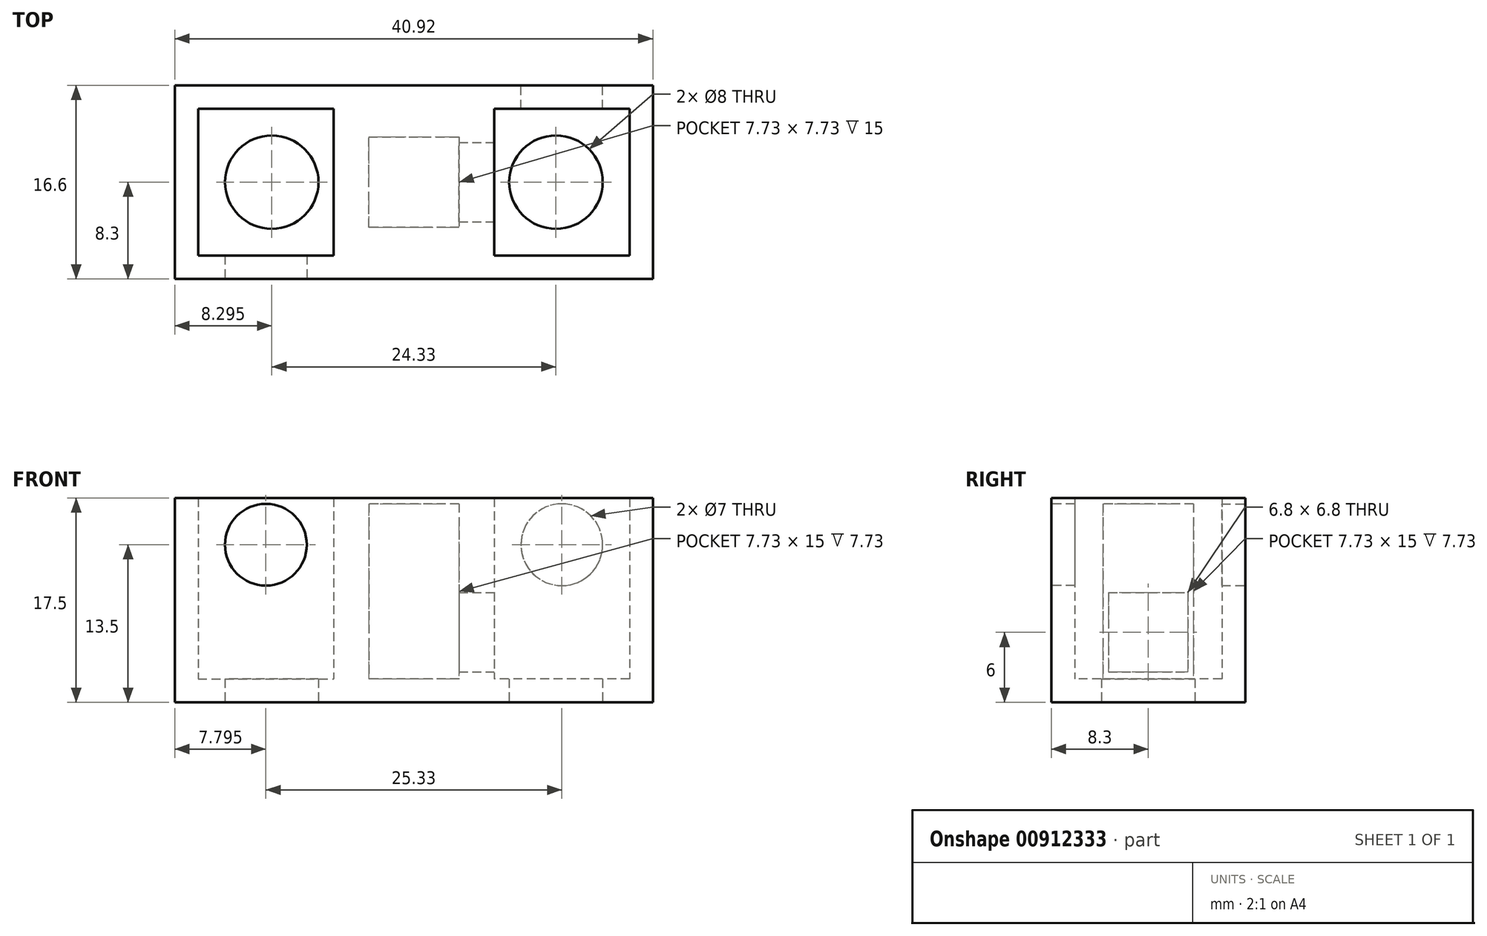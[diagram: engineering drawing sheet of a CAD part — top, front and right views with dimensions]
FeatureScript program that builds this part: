
annotation { "Feature Type Name" : "Feature", "Feature Type Description" : "" }
export const myFeature = defineFeature(function(context is Context, id is Id, definition is map)
    precondition{}
    {
        {
            var Q0;
            Q0=qCreatedBy(makeId("Top.planeOp"),FACE);
            var sketch = newSketch(context, id + "F0", { "sketchPlane" : qUnion([Q0])});
            skLineSegment(sketch, "E0.bottom", {"start": v(-3.17, 3.17) * mm, "end": v(3.16, 3.17) * mm});
            skLineSegment(sketch, "E0.top", {"start": v(-3.17, -3.17) * mm, "end": v(3.17, -3.17) * mm});
            skLineSegment(sketch, "E0.left", {"start": v(-3.17, 3.17) * mm, "end": v(-3.17, -3.17) * mm});
            skLineSegment(sketch, "E0.right", {"start": v(3.17, 3.17) * mm, "end": v(3.17, -3.17) * mm});
            skLineSegment(sketch, "E1", {"start": v(-3.17, 0) * mm, "end": v(3.17, 0) * mm, "construction": true});
            skLineSegment(sketch, "E2", {"start": v(-3.17, 3.17) * mm, "end": v(-3.87, 3.17) * mm, "construction": true});
            skLineSegment(sketch, "E3", {"start": v(-3.17, 3.17) * mm, "end": v(-3.17, 3.86) * mm, "construction": true});
            skLineSegment(sketch, "E4", {"start": v(-3.87, 3.86) * mm, "end": v(3.86, 3.86) * mm});
            skLineSegment(sketch, "E5", {"start": v(3.86, 3.86) * mm, "end": v(3.86, -3.86) * mm});
            skLineSegment(sketch, "E6", {"start": v(3.86, -3.86) * mm, "end": v(-3.86, -3.86) * mm});
            skLineSegment(sketch, "E7", {"start": v(-3.86, -3.86) * mm, "end": v(-3.87, 3.87) * mm});
            skLineSegment(sketch, "E8", {"start": v(3.17, -3.17) * mm, "end": v(3.17, -3.86) * mm, "construction": true});
            skLineSegment(sketch, "E9", {"start": v(-3.87, 3.17) * mm, "end": v(-6.87, 3.17) * mm, "construction": true});
            skLineSegment(sketch, "E10", {"start": v(3.17, -3.86) * mm, "end": v(3.17, -6.87) * mm, "construction": true});
            skLineSegment(sketch, "E11", {"start": v(-3.17, 3.86) * mm, "end": v(-3.17, 6.87) * mm, "construction": true});
            skLineSegment(sketch, "E12", {"start": v(-6.87, 6.87) * mm, "end": v(6.86, 6.87) * mm});
            skLineSegment(sketch, "E13", {"start": v(6.86, 6.87) * mm, "end": v(6.86, -6.87) * mm});
            skLineSegment(sketch, "E14", {"start": v(6.86, -6.87) * mm, "end": v(-6.87, -6.87) * mm});
            skLineSegment(sketch, "E15", {"start": v(-6.86, -6.86) * mm, "end": v(-6.87, 6.86) * mm});
            skLineSegment(sketch, "E16", {"start": v(-12.17, 5.3) * mm, "end": v(-12.17, -5.3) * mm, "construction": true});
            skLineSegment(sketch, "E17", {"start": v(-17.46, 0) * mm, "end": v(-6.87, 0) * mm, "construction": true});
            skLineSegment(sketch, "E18", {"start": v(0, 3.17) * mm, "end": v(0, -3.17) * mm, "construction": true});
            skCircle(sketch, "E19", {"center": v(-12.17, 0) * mm, "radius": 4 * mm});
            skLineSegment(sketch, "E20", {"start": v(0, 0) * mm, "end": v(-6.86, 0) * mm, "construction": true});
            skLineSegment(sketch, "E21.bottom", {"start": v(-17.46, 5.3) * mm, "end": v(-6.87, 5.3) * mm});
            skLineSegment(sketch, "E21.top", {"start": v(-17.46, -5.3) * mm, "end": v(-6.86, -5.3) * mm});
            skLineSegment(sketch, "E21.left", {"start": v(-17.46, 5.3) * mm, "end": v(-17.46, -5.3) * mm});
            skLineSegment(sketch, "E21.right", {"start": v(-6.87, 5.3) * mm, "end": v(-6.86, -5.3) * mm});
            skLineSegment(sketch, "E22", {"start": v(-17.46, 5.3) * mm, "end": v(-17.46, 6.3) * mm, "construction": true});
            skLineSegment(sketch, "E23", {"start": v(-17.46, 5.3) * mm, "end": v(-18.47, 5.3) * mm, "construction": true});
            skLineSegment(sketch, "E24", {"start": v(-18.47, 6.3) * mm, "end": v(-18.47, -6.3) * mm});
            skLineSegment(sketch, "E25", {"start": v(-18.47, 6.3) * mm, "end": v(-6.87, 6.3) * mm});
            skLineSegment(sketch, "E26", {"start": v(-6.87, 6.3) * mm, "end": v(-6.87, 6.87) * mm});
            skLineSegment(sketch, "E27.MirrorCS", {"start": v(-18.47, -6.3) * mm, "end": v(-6.86, -6.3) * mm});
            skLineSegment(sketch, "E28", {"start": v(-6.86, -6.3) * mm, "end": v(-6.86, -6.86) * mm});
            skLineSegment(sketch, "E29", {"start": v(-18.47, 6.3) * mm, "end": v(-18.47, 8.3) * mm, "construction": true});
            skLineSegment(sketch, "E30", {"start": v(-18.47, 6.3) * mm, "end": v(-20.47, 6.3) * mm, "construction": true});
            skLineSegment(sketch, "E31", {"start": v(-20.47, 8.3) * mm, "end": v(20.47, 8.3) * mm});
            skLineSegment(sketch, "E32", {"start": v(-20.47, 8.3) * mm, "end": v(-20.47, -8.3) * mm});
            skLineSegment(sketch, "E33", {"start": v(-18.47, -6.3) * mm, "end": v(-18.47, -8.3) * mm, "construction": true});
            skLineSegment(sketch, "E34.MirrorCS", {"start": v(6.86, 6.3) * mm, "end": v(6.86, 6.87) * mm});
            skLineSegment(sketch, "E35.MirrorCS", {"start": v(18.47, 6.3) * mm, "end": v(6.86, 6.3) * mm});
            skLineSegment(sketch, "E36.MirrorCS", {"start": v(18.47, 6.3) * mm, "end": v(18.47, -6.3) * mm});
            skLineSegment(sketch, "E37.MirrorCS", {"start": v(18.47, -6.3) * mm, "end": v(6.86, -6.3) * mm});
            skLineSegment(sketch, "E38.MirrorCS", {"start": v(6.87, -6.3) * mm, "end": v(6.87, -6.86) * mm});
            skLineSegment(sketch, "E39.MirrorCS", {"start": v(17.46, -5.3) * mm, "end": v(6.86, -5.3) * mm});
            skLineSegment(sketch, "E40.MirrorCS", {"start": v(17.46, 5.3) * mm, "end": v(17.47, -5.3) * mm});
            skCircle(sketch, "E41.MirrorC", {"center": v(12.17, 0) * mm, "radius": 4 * mm});
            skLineSegment(sketch, "E42.MirrorCS", {"start": v(17.46, 5.3) * mm, "end": v(6.86, 5.3) * mm});
            skLineSegment(sketch, "E43.MirrorCS", {"start": v(20.47, 8.3) * mm, "end": v(20.47, -8.3) * mm});
            skLineSegment(sketch, "E44.MirrorCS", {"start": v(-20.47, -8.3) * mm, "end": v(20.47, -8.3) * mm});
            skSolve(sketch);
        }
        {
            var Q0;
            {var subQ0=sQuery(id+"F0.wireOp",EDGE,"E39.MirrorCS");Q0=makeQuery(id+"F0.imprint","IMPRINT",FACE,{"disambiguationData":[TD([[makeQuery(id+"F0.imprint","IMPRINT",EDGE,{"derivedFrom":subQ0}),-1.0]])]});}
            var Q1;
            {var subQ0=sQuery(id+"F0.wireOp",EDGE,"E34.MirrorCS");Q1=makeQuery(id+"F0.imprint","IMPRINT",FACE,{"disambiguationData":[TD([[makeQuery(id+"F0.imprint","IMPRINT",EDGE,{"derivedFrom":subQ0}),-1.0]])]});}
            var Q2;
            Q2=makeQuery(id+"F0.imprint","IMPRINT",FACE,{"disambiguationData":[TD([[makeQuery(id+"F0.imprint","IMPRINT",EDGE,{"derivedFrom":sQuery(id+"F0.wireOp",EDGE,"E12")}),1.0]])]});
            var Q3;
            {var subQ1=sQuery(id+"F0.wireOp",EDGE,"E21.bottom");Q3=makeQuery(id+"F0.imprint","IMPRINT",FACE,{"disambiguationData":[TD([[makeQuery(id+"F0.imprint","IMPRINT",EDGE,{"derivedFrom":subQ1}),1.0]])]});}
            var Q4;
            Q4=makeQuery(id+"F0.imprint","IMPRINT",FACE,{"disambiguationData":[TD([[makeQuery(id+"F0.imprint","IMPRINT",EDGE,{"derivedFrom":sQuery(id+"F0.wireOp",EDGE,"E19")}),-1.0]])]});
            var Q5;
            Q5=makeQuery(id+"F0.imprint","IMPRINT",FACE,{"disambiguationData":[TD([[makeQuery(id+"F0.imprint","IMPRINT",EDGE,{"derivedFrom":sQuery(id+"F0.wireOp",EDGE,"E4")}),1.0]])]});
            var Q6;
            Q6=makeQuery(id+"F0.imprint","IMPRINT",FACE,{"disambiguationData":[TD([[makeQuery(id+"F0.imprint","IMPRINT",EDGE,{"derivedFrom":sQuery(id+"F0.wireOp",EDGE,"E0.bottom")}),1.0]])]});
            var Q7;
            Q7=makeQuery(id+"F0.imprint","IMPRINT",FACE,{"disambiguationData":[TD([[makeQuery(id+"F0.imprint","IMPRINT",EDGE,{"derivedFrom":sQuery(id+"F0.wireOp",EDGE,"E0.bottom")}),-1.0]])]});
            var Q8;
            {var subQ0=sQuery(id+"F0.wireOp",EDGE,"E35.MirrorCS");Q8=makeQuery(id+"F0.imprint","IMPRINT",FACE,{"disambiguationData":[TD([[makeQuery(id+"F0.imprint","IMPRINT",EDGE,{"derivedFrom":subQ0}),1.0]])]});}
            extrude(context, id + "F1", {"entities" : qUnion([Q0, Q1, Q2, Q3, Q4, Q5, Q6, Q7, Q8]), "depth" : 2 * mm, "offsetDistance" : 25 * mm});
        }
        {
            var Q0;
            Q0=makeQuery(id+"F1.opExtrude","CAP_FACE",FACE,{"disambiguationData":[OSD([sQuery(id+"F0.wireOp",EDGE,"E19"),sQuery(id+"F0.wireOp",EDGE,"E31"),sQuery(id+"F0.wireOp",EDGE,"E32"),sQuery(id+"F0.wireOp",EDGE,"E41.MirrorC"),sQuery(id+"F0.wireOp",EDGE,"E43.MirrorCS"),sQuery(id+"F0.wireOp",EDGE,"E44.MirrorCS")])],"isStart":false});
            var sketch = newSketch(context, id + "F2", { "sketchPlane" : qUnion([Q0])});
            skLineSegment(sketch, "E45.0", {"start": v(-18.47, 6.3) * mm, "end": v(-18.47, -6.3) * mm});
            skLineSegment(sketch, "E45.1", {"start": v(-18.47, 6.3) * mm, "end": v(-6.87, 6.3) * mm});
            skLineSegment(sketch, "E45.2", {"start": v(-18.47, -6.3) * mm, "end": v(-6.86, -6.3) * mm});
            skLineSegment(sketch, "E45.3", {"start": v(-6.86, -6.86) * mm, "end": v(-6.87, 6.86) * mm});
            skLineSegment(sketch, "E45.4", {"start": v(-6.87, 6.3) * mm, "end": v(-6.87, 6.87) * mm});
            skLineSegment(sketch, "E45.5", {"start": v(-6.86, -6.3) * mm, "end": v(-6.86, -6.86) * mm});
            skLineSegment(sketch, "E45.6", {"start": v(-3.87, 3.86) * mm, "end": v(3.86, 3.86) * mm});
            skLineSegment(sketch, "E45.7", {"start": v(-3.86, -3.86) * mm, "end": v(-3.87, 3.87) * mm});
            skLineSegment(sketch, "E45.8", {"start": v(3.86, -3.86) * mm, "end": v(-3.86, -3.86) * mm});
            skLineSegment(sketch, "E45.9", {"start": v(3.86, 3.86) * mm, "end": v(3.86, -3.86) * mm});
            skLineSegment(sketch, "E45.10", {"start": v(6.86, 6.87) * mm, "end": v(6.86, -6.87) * mm});
            skLineSegment(sketch, "E45.11", {"start": v(18.47, 6.3) * mm, "end": v(6.86, 6.3) * mm});
            skLineSegment(sketch, "E45.12", {"start": v(18.47, 6.3) * mm, "end": v(18.47, -6.3) * mm});
            skLineSegment(sketch, "E45.13", {"start": v(18.47, -6.3) * mm, "end": v(6.86, -6.3) * mm});
            skLineSegment(sketch, "E45.14", {"start": v(6.87, -6.3) * mm, "end": v(6.87, -6.86) * mm});
            skLineSegment(sketch, "E45.15", {"start": v(6.86, 6.3) * mm, "end": v(6.86, 6.87) * mm});
            skLineSegment(sketch, "E46.0", {"start": v(-20.47, 8.3) * mm, "end": v(20.47, 8.3) * mm});
            skLineSegment(sketch, "E46.1", {"start": v(-20.47, 8.3) * mm, "end": v(-20.47, -8.3) * mm});
            skLineSegment(sketch, "E46.2", {"start": v(-20.47, -8.3) * mm, "end": v(20.47, -8.3) * mm});
            skLineSegment(sketch, "E46.3", {"start": v(20.47, 8.3) * mm, "end": v(20.47, -8.3) * mm});
            skSolve(sketch);
        }
        {
            var Q0;
            Q0=makeQuery(id+"F2.imprint","IMPRINT",FACE,{"disambiguationData":[TD([[makeQuery(id+"F2.imprint","IMPRINT",EDGE,{"derivedFrom":sQuery(id+"F2.wireOp",EDGE,"E45.0")}),-1.0]])]});
            extrude(context, id + "F3", {"entities" : qUnion([Q0]), "operationType" : NewBodyOperationType.ADD, "depth" : 15 * mm, "offsetDistance" : 25 * mm});
        }
        {
            var Q0;
            Q0=makeQuery(id+"F3.opExtrude","CAP_FACE",FACE,{"disambiguationData":[OSD([sQuery(id+"F2.wireOp",EDGE,"E45.0"),sQuery(id+"F2.wireOp",EDGE,"E45.1"),sQuery(id+"F2.wireOp",EDGE,"E45.2"),sQuery(id+"F2.wireOp",EDGE,"E45.3"),sQuery(id+"F2.wireOp",EDGE,"E45.4"),sQuery(id+"F2.wireOp",EDGE,"E45.5"),sQuery(id+"F2.wireOp",EDGE,"E45.6"),sQuery(id+"F2.wireOp",EDGE,"E45.7"),sQuery(id+"F2.wireOp",EDGE,"E45.8"),sQuery(id+"F2.wireOp",EDGE,"E45.9"),sQuery(id+"F2.wireOp",EDGE,"E45.10"),sQuery(id+"F2.wireOp",EDGE,"E45.11"),sQuery(id+"F2.wireOp",EDGE,"E45.12"),sQuery(id+"F2.wireOp",EDGE,"E45.13"),sQuery(id+"F2.wireOp",EDGE,"E45.14"),sQuery(id+"F2.wireOp",EDGE,"E45.15"),sQuery(id+"F2.wireOp",EDGE,"E46.0"),sQuery(id+"F2.wireOp",EDGE,"E46.1"),sQuery(id+"F2.wireOp",EDGE,"E46.2"),sQuery(id+"F2.wireOp",EDGE,"E46.3")])],"isStart":false});
            var sketch = newSketch(context, id + "F4", { "sketchPlane" : qUnion([Q0])});
            skLineSegment(sketch, "E47.0", {"start": v(-20.47, 8.3) * mm, "end": v(-20.47, -8.3) * mm});
            skLineSegment(sketch, "E47.1", {"start": v(-20.47, 8.3) * mm, "end": v(20.47, 8.3) * mm});
            skLineSegment(sketch, "E47.2", {"start": v(20.47, 8.3) * mm, "end": v(20.47, -8.3) * mm});
            skLineSegment(sketch, "E47.3", {"start": v(-20.47, -8.3) * mm, "end": v(20.47, -8.3) * mm});
            skLineSegment(sketch, "E47.4", {"start": v(18.47, 6.3) * mm, "end": v(18.47, -6.3) * mm});
            skLineSegment(sketch, "E47.5", {"start": v(18.47, -6.3) * mm, "end": v(6.86, -6.3) * mm});
            skLineSegment(sketch, "E47.6", {"start": v(6.86, 6.87) * mm, "end": v(6.86, -6.87) * mm});
            skLineSegment(sketch, "E47.7", {"start": v(6.87, -6.3) * mm, "end": v(6.87, -6.86) * mm});
            skLineSegment(sketch, "E47.8", {"start": v(18.47, 6.3) * mm, "end": v(6.86, 6.3) * mm});
            skLineSegment(sketch, "E47.9", {"start": v(6.86, 6.3) * mm, "end": v(6.86, 6.87) * mm});
            skLineSegment(sketch, "E47.10", {"start": v(-6.86, -6.86) * mm, "end": v(-6.87, 6.86) * mm});
            skLineSegment(sketch, "E47.11", {"start": v(-18.47, -6.3) * mm, "end": v(-6.86, -6.3) * mm});
            skLineSegment(sketch, "E47.12", {"start": v(-18.47, 6.3) * mm, "end": v(-18.47, -6.3) * mm});
            skLineSegment(sketch, "E47.13", {"start": v(-18.47, 6.3) * mm, "end": v(-6.87, 6.3) * mm});
            skLineSegment(sketch, "E47.14", {"start": v(-6.87, 6.3) * mm, "end": v(-6.87, 6.87) * mm});
            skLineSegment(sketch, "E47.15", {"start": v(-6.86, -6.3) * mm, "end": v(-6.86, -6.86) * mm});
            skSolve(sketch);
        }
        {
            var Q0;
            Q0=makeQuery(id+"F4.imprint","IMPRINT",FACE,{"disambiguationData":[TD([[makeQuery(id+"F4.imprint","IMPRINT",EDGE,{"derivedFrom":sQuery(id+"F4.wireOp",EDGE,"E47.0")}),1.0]])]});
            var Q1;
            Q1=makeQuery(id+"F4.imprint","IMPRINT",FACE,{"disambiguationData":[TD([[makeQuery(id+"F4.imprint","IMPRINT",EDGE,{"derivedFrom":makeQuery(id+"F3.opExtrude","CAP_EDGE",EDGE,{"disambiguationData":[OSD([sQuery(id+"F2.wireOp",EDGE,"E45.6")])],"isStart":false})}),-1.0]])]});
            extrude(context, id + "F5", {"entities" : qUnion([Q0, Q1]), "operationType" : NewBodyOperationType.ADD, "depth" : 0.5 * mm, "offsetDistance" : 25 * mm});
        }
        {
            var Q0;
            Q0=makeQuery(id+"F5.boolean.opBoolean","MERGE",FACE,{"derivedFrom":[makeQuery(id+"F3.opExtrude","SWEPT_FACE",FACE,{"disambiguationData":[OSD([sQuery(id+"F2.wireOp",EDGE,"E45.10"),sQuery(id+"F2.wireOp",EDGE,"E45.14"),sQuery(id+"F2.wireOp",EDGE,"E45.15")])]}),makeQuery(id+"F5.opExtrude","SWEPT_FACE",FACE,{"disambiguationData":[OSD([sQuery(id+"F4.wireOp",EDGE,"E47.6"),sQuery(id+"F4.wireOp",EDGE,"E47.7"),sQuery(id+"F4.wireOp",EDGE,"E47.9")])]})]});
            var sketch = newSketch(context, id + "F6", { "sketchPlane" : qUnion([Q0])});
            skLineSegment(sketch, "E48.0", {"start": v(-3.86, 17) * mm, "end": v(-3.86, 2) * mm, "construction": true});
            skLineSegment(sketch, "E49.0", {"start": v(3.86, 17) * mm, "end": v(-3.86, 17) * mm, "construction": true});
            skLineSegment(sketch, "E50.bottom", {"start": v(-3.4, 9.4) * mm, "end": v(3.4, 9.4) * mm});
            skLineSegment(sketch, "E50.top", {"start": v(-3.4, 2.6) * mm, "end": v(3.4, 2.6) * mm});
            skLineSegment(sketch, "E50.left", {"start": v(-3.4, 9.4) * mm, "end": v(-3.4, 2.6) * mm});
            skLineSegment(sketch, "E50.right", {"start": v(3.4, 9.4) * mm, "end": v(3.4, 2.6) * mm});
            skLineSegment(sketch, "E51", {"start": v(-3.4, 6) * mm, "end": v(3.4, 6) * mm, "construction": true});
            skLineSegment(sketch, "E52", {"start": v(0, 17) * mm, "end": v(0, 6) * mm});
            skSolve(sketch);
        }
        {
            var Q0;
            Q0 = qSketchRegion(id + "F6", true);
            extrude(context, id + "F7", {"entities" : qUnion([Q0]), "operationType" : NewBodyOperationType.REMOVE, "oppositeDirection" : true, "depth" : 4 * mm, "offsetDistance" : 25 * mm});
        }
        {
            var Q0;
            Q0=makeQuery(id+"F5.boolean.opBoolean","MERGE",FACE,{"derivedFrom":[makeQuery(id+"F3.boolean.opBoolean","MERGE",FACE,{"derivedFrom":[makeQuery(id+"F1.opExtrude","SWEPT_FACE",FACE,{"disambiguationData":[OSD([sQuery(id+"F0.wireOp",EDGE,"E31")])]}),makeQuery(id+"F3.opExtrude","SWEPT_FACE",FACE,{"disambiguationData":[OSD([sQuery(id+"F2.wireOp",EDGE,"E46.0")])]})]}),makeQuery(id+"F5.opExtrude","SWEPT_FACE",FACE,{"disambiguationData":[OSD([sQuery(id+"F4.wireOp",EDGE,"E47.1")])]})]});
            var sketch = newSketch(context, id + "F8", { "sketchPlane" : qUnion([Q0])});
            skLineSegment(sketch, "E53.0", {"start": v(-18.47, 17.5) * mm, "end": v(-6.87, 17.5) * mm, "construction": true});
            skLineSegment(sketch, "E54", {"start": v(-12.67, 17.5) * mm, "end": v(-12.67, 17) * mm, "construction": true});
            skLineSegment(sketch, "E55", {"start": v(-12.67, 17) * mm, "end": v(-12.67, 13.5) * mm, "construction": true});
            skCircle(sketch, "E56", {"center": v(-12.67, 13.5) * mm, "radius": 3.5 * mm});
            skSolve(sketch);
        }
        {
            var Q0;
            Q0=makeQuery(id+"F8.imprint","IMPRINT",FACE,{"disambiguationData":[TD([[makeQuery(id+"F8.imprint","IMPRINT",EDGE,{"derivedFrom":sQuery(id+"F8.wireOp",EDGE,"E56")}),1.0]])]});
            extrude(context, id + "F9", {"entities" : qUnion([Q0]), "operationType" : NewBodyOperationType.REMOVE, "oppositeDirection" : true, "depth" : 3 * mm, "offsetDistance" : 25 * mm});
        }
        {
            var Q0;
            Q0=makeQuery(id+"F5.boolean.opBoolean","MERGE",FACE,{"derivedFrom":[makeQuery(id+"F3.boolean.opBoolean","MERGE",FACE,{"derivedFrom":[makeQuery(id+"F1.opExtrude","SWEPT_FACE",FACE,{"disambiguationData":[OSD([sQuery(id+"F0.wireOp",EDGE,"E44.MirrorCS")])]}),makeQuery(id+"F3.opExtrude","SWEPT_FACE",FACE,{"disambiguationData":[OSD([sQuery(id+"F2.wireOp",EDGE,"E46.2")])]})]}),makeQuery(id+"F5.opExtrude","SWEPT_FACE",FACE,{"disambiguationData":[OSD([sQuery(id+"F4.wireOp",EDGE,"E47.3")])]})]});
            var sketch = newSketch(context, id + "F10", { "sketchPlane" : qUnion([Q0])});
            skLineSegment(sketch, "E57.0", {"start": v(-18.47, 17.5) * mm, "end": v(-6.87, 17.5) * mm, "construction": true});
            skLineSegment(sketch, "E58", {"start": v(-12.67, 17.5) * mm, "end": v(-12.67, 17) * mm, "construction": true});
            skLineSegment(sketch, "E59", {"start": v(-12.67, 17) * mm, "end": v(-12.67, 13.5) * mm, "construction": true});
            skCircle(sketch, "E60", {"center": v(-12.67, 13.5) * mm, "radius": 3.5 * mm});
            skSolve(sketch);
        }
        {
            var Q0;
            Q0=makeQuery(id+"F10.imprint","IMPRINT",FACE,{"disambiguationData":[TD([[makeQuery(id+"F10.imprint","IMPRINT",EDGE,{"derivedFrom":sQuery(id+"F10.wireOp",EDGE,"E60")}),1.0]])]});
            extrude(context, id + "F11", {"entities" : qUnion([Q0]), "operationType" : NewBodyOperationType.REMOVE, "oppositeDirection" : true, "depth" : 3 * mm, "offsetDistance" : 25 * mm});
        }
    });
